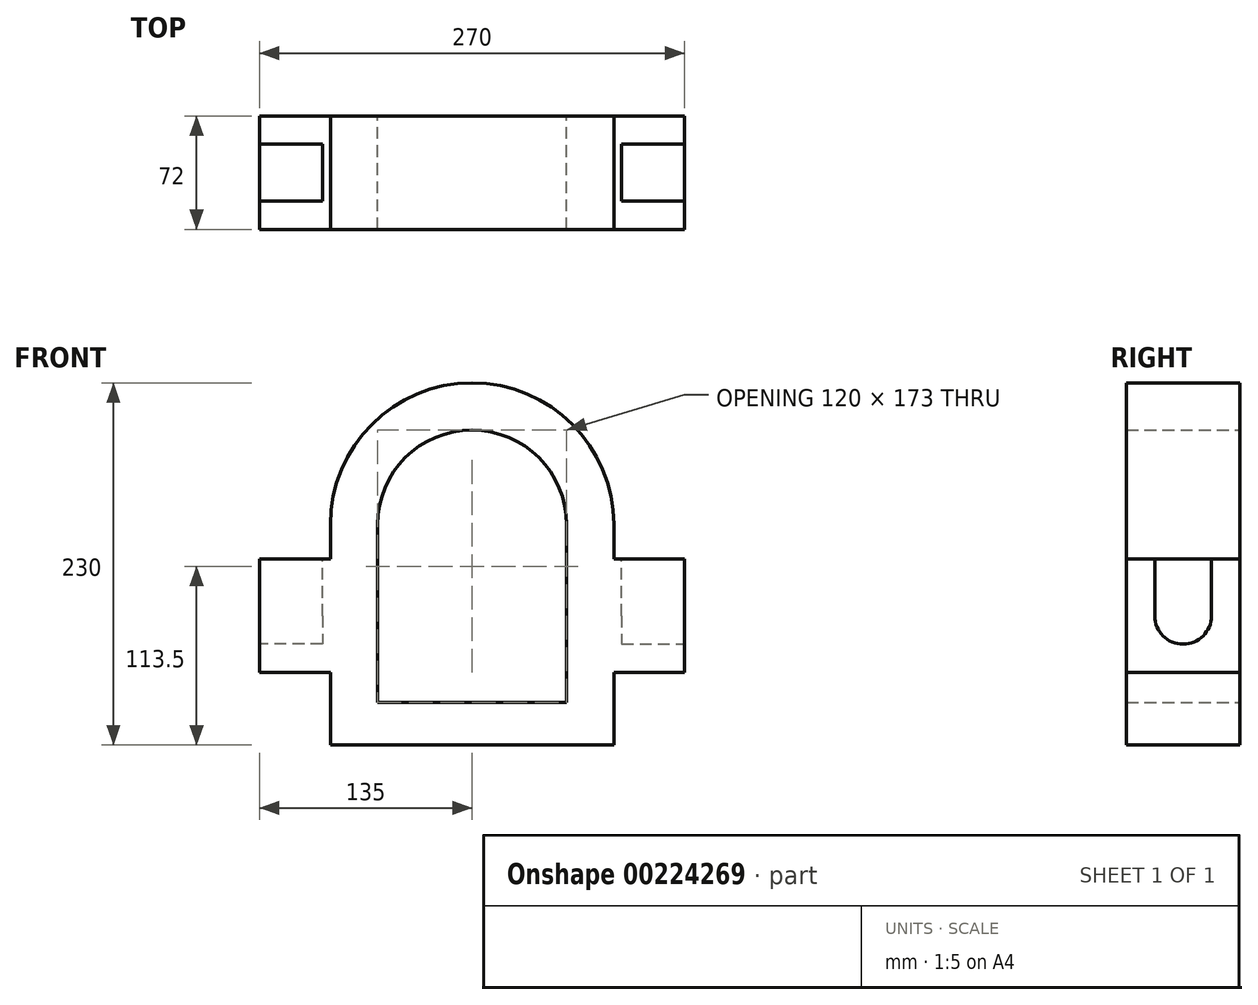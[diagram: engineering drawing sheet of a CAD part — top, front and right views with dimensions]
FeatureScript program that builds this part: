
annotation { "Feature Type Name" : "Feature", "Feature Type Description" : "" }
export const myFeature = defineFeature(function(context is Context, id is Id, definition is map)
    precondition{}
    {
        {
            var Q0;
            Q0=qCreatedBy(makeId("Front.planeOp"),FACE);
            var sketch = newSketch(context, id + "F0", { "sketchPlane" : qUnion([Q0])});
            skArc(sketch, "E0", {"start": v(90, 0) * mm, "mid": v(0, 90) * mm, "end": v(-90, 0) * mm});
            skArc(sketch, "E1", {"start": v(60, 0) * mm, "mid": v(0, 60) * mm, "end": v(-60, 0) * mm});
            skLineSegment(sketch, "E2", {"start": v(-90, 0) * mm, "end": v(-90, -22) * mm});
            skLineSegment(sketch, "E3", {"start": v(-90, -22) * mm, "end": v(-135, -22) * mm});
            skLineSegment(sketch, "E4", {"start": v(-135, -22) * mm, "end": v(-135, -94) * mm});
            skLineSegment(sketch, "E5", {"start": v(-135, -94) * mm, "end": v(-90, -94) * mm});
            skLineSegment(sketch, "E6", {"start": v(-90, -94) * mm, "end": v(-90, -140) * mm});
            skLineSegment(sketch, "E7.MirrorCS", {"start": v(90, 0) * mm, "end": v(90, -22) * mm});
            skLineSegment(sketch, "E8.MirrorCS", {"start": v(90, -22) * mm, "end": v(135, -22) * mm});
            skLineSegment(sketch, "E9.MirrorCS", {"start": v(135, -22) * mm, "end": v(135, -94) * mm});
            skLineSegment(sketch, "E10.MirrorCS", {"start": v(135, -94) * mm, "end": v(90, -94) * mm});
            skLineSegment(sketch, "E11.MirrorCS", {"start": v(90, -94) * mm, "end": v(90, -140) * mm});
            skLineSegment(sketch, "E12", {"start": v(-90, -140) * mm, "end": v(90, -140) * mm});
            skLineSegment(sketch, "E13", {"start": v(-60, 0) * mm, "end": v(-60, -113) * mm});
            skLineSegment(sketch, "E14", {"start": v(-60, -113) * mm, "end": v(60, -113) * mm});
            skLineSegment(sketch, "E15", {"start": v(60, -113) * mm, "end": v(60, 0) * mm});
            skSolve(sketch);
        }
        {
            var Q0;
            Q0 = qSketchRegion(id + "F0", true);
            extrude(context, id + "F1", {"entities" : qUnion([Q0]), "endBound" : BoundingType.SYMMETRIC, "depth" : 72 * mm});
        }
        {
            var Q0;
            Q0=makeQuery(id+"F1.opExtrude","SWEPT_FACE",FACE,{"disambiguationData":[OSD([sQuery(id+"F0.wireOp",EDGE,"E8.MirrorCS")])]});
            var sketch = newSketch(context, id + "F2", { "sketchPlane" : qUnion([Q0])});
            skLineSegment(sketch, "E16", {"start": v(135, 18) * mm, "end": v(95, 18) * mm});
            skLineSegment(sketch, "E17", {"start": v(95, 18) * mm, "end": v(95, -18) * mm});
            skLineSegment(sketch, "E18", {"start": v(95, -18) * mm, "end": v(135, -18) * mm});
            skLineSegment(sketch, "E19", {"start": v(135, -18) * mm, "end": v(135, 18) * mm});
            skLineSegment(sketch, "E20.MirrorCS", {"start": v(-135, 18) * mm, "end": v(-95, 18) * mm});
            skLineSegment(sketch, "E21.MirrorCS", {"start": v(-95, -18) * mm, "end": v(-135, -18) * mm});
            skLineSegment(sketch, "E22.MirrorCS", {"start": v(-95, 18) * mm, "end": v(-95, -18) * mm});
            skLineSegment(sketch, "E23.MirrorCS", {"start": v(-135, -18) * mm, "end": v(-135, 18) * mm});
            skSolve(sketch);
        }
        {
            var Q0;
            Q0=makeQuery(id+"F1.opExtrude","SWEPT_FACE",FACE,{"disambiguationData":[OSD([sQuery(id+"F0.wireOp",EDGE,"E9.MirrorCS")])]});
            var sketch = newSketch(context, id + "F3", { "sketchPlane" : qUnion([Q0])});
            skArc(sketch, "E24", {"start": v(-18, -58) * mm, "mid": v(0, -76) * mm, "end": v(18, -58) * mm});
            skLineSegment(sketch, "E25", {"start": v(-18, -58) * mm, "end": v(18, -58) * mm});
            skSolve(sketch);
        }
        {
            var Q0;
            Q0=makeQuery(id+"F1.opExtrude","SWEPT_FACE",FACE,{"disambiguationData":[OSD([sQuery(id+"F0.wireOp",EDGE,"E4")])]});
            var sketch = newSketch(context, id + "F4", { "sketchPlane" : qUnion([Q0])});
            skLineSegment(sketch, "E26.0", {"start": v(18, -58) * mm, "end": v(-18, -58) * mm});
            skArc(sketch, "E27.0", {"start": v(18, -58) * mm, "mid": v(0, -76) * mm, "end": v(-18, -58) * mm});
            skSolve(sketch);
        }
        {
            var Q0;
            Q0=makeQuery(id+"F2.imprint","IMPRINT",FACE,{"disambiguationData":[TD([[makeQuery(id+"F2.imprint","IMPRINT",EDGE,{"derivedFrom":sQuery(id+"F2.wireOp",EDGE,"E20.MirrorCS")}),-1.0]])]});
            var Q1;
            Q1=makeQuery(id+"F2.imprint","IMPRINT",FACE,{"disambiguationData":[TD([[makeQuery(id+"F2.imprint","IMPRINT",EDGE,{"derivedFrom":sQuery(id+"F2.wireOp",EDGE,"E16")}),1.0]])]});
            extrude(context, id + "F5", {"entities" : qUnion([Q0, Q1]), "operationType" : NewBodyOperationType.REMOVE, "oppositeDirection" : true, "depth" : 36 * mm});
        }
        {
            var Q0;
            Q0=makeQuery(id+"F3.imprint","IMPRINT",FACE,{"disambiguationData":[TD([[makeQuery(id+"F3.imprint","IMPRINT",EDGE,{"derivedFrom":sQuery(id+"F3.wireOp",EDGE,"E24")}),1.0]])]});
            extrude(context, id + "F6", {"entities" : qUnion([Q0]), "operationType" : NewBodyOperationType.REMOVE, "oppositeDirection" : true, "depth" : 40 * mm});
        }
        {
            var Q0;
            Q0=makeQuery(id+"F4.imprint","IMPRINT",FACE,{"disambiguationData":[TD([[makeQuery(id+"F4.imprint","IMPRINT",EDGE,{"derivedFrom":sQuery(id+"F4.wireOp",EDGE,"E26.0")}),1.0]])]});
            extrude(context, id + "F7", {"entities" : qUnion([Q0]), "operationType" : NewBodyOperationType.REMOVE, "oppositeDirection" : true, "depth" : 40 * mm});
        }
    });
